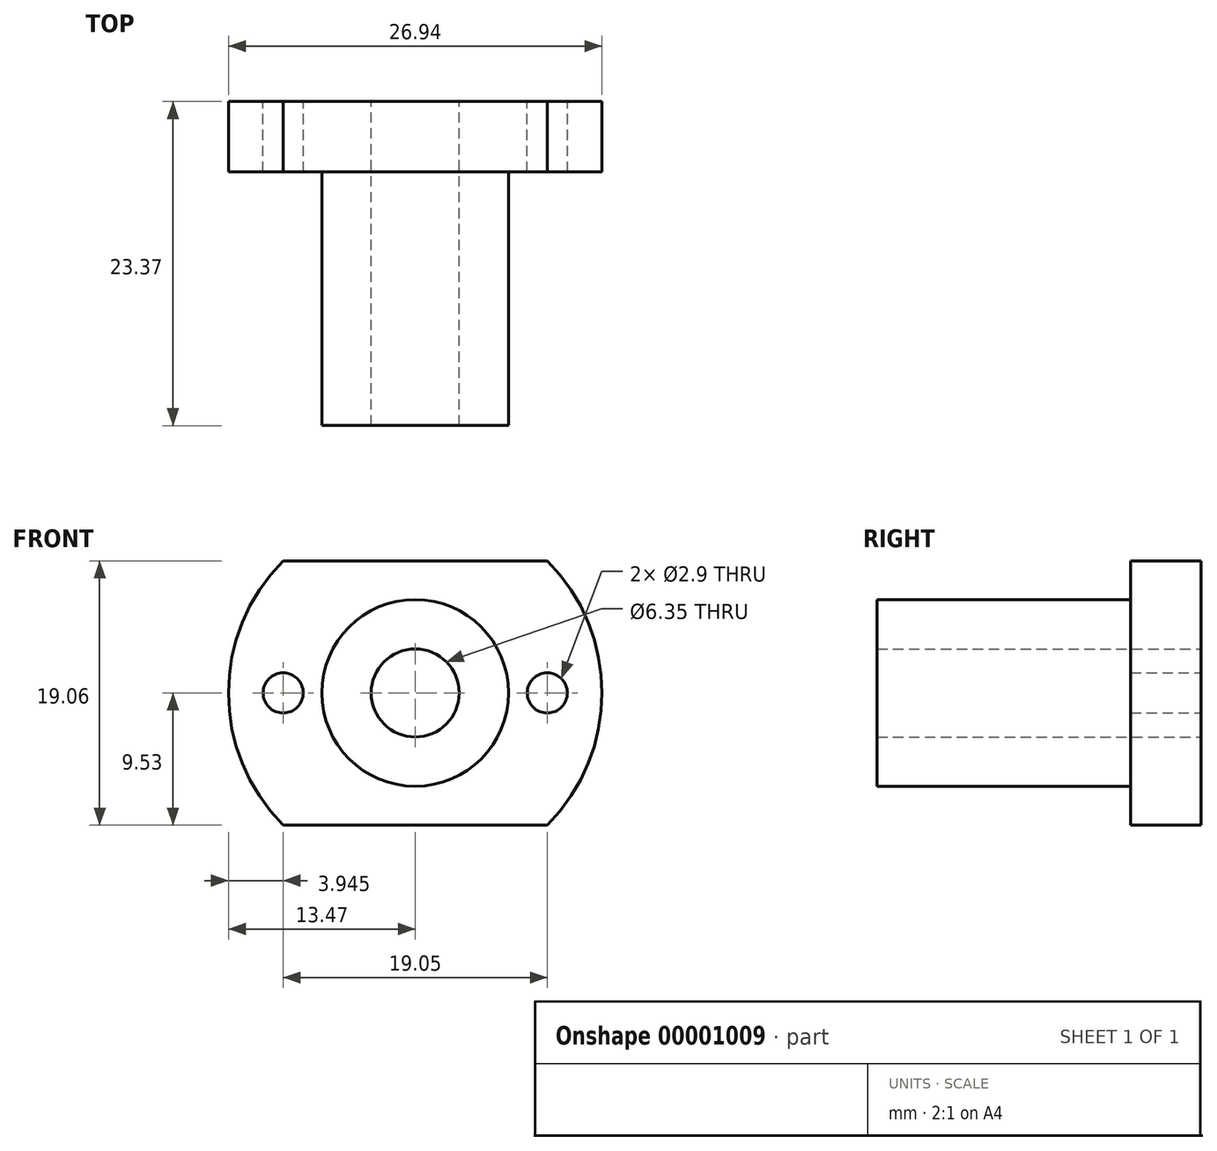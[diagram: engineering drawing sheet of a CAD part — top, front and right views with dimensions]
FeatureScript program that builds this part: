
annotation { "Feature Type Name" : "Feature", "Feature Type Description" : "" }
export const myFeature = defineFeature(function(context is Context, id is Id, definition is map)
    precondition{}
    {
        {
            var Q0;
            Q0=qCreatedBy(makeId("Front.planeOp"),FACE);
            var sketch = newSketch(context, id + "F0", { "sketchPlane" : qUnion([Q0])});
            skLineSegment(sketch, "E0.bottom", {"start": v(-9.53, 9.53) * mm, "end": v(9.53, 9.53) * mm});
            skLineSegment(sketch, "E0.top", {"start": v(-9.52, -9.53) * mm, "end": v(9.53, -9.52) * mm});
            skCircle(sketch, "E1", {"center": v(-9.53, 0) * mm, "radius": 1.45 * mm});
            skCircle(sketch, "E2", {"center": v(9.53, 0) * mm, "radius": 1.45 * mm});
            skArc(sketch, "E3", {"start": v(-9.53, 9.52) * mm, "mid": v(-13.47, 0) * mm, "end": v(-9.52, -9.53) * mm});
            skArc(sketch, "E4.trimOffspring", {"start": v(9.52, -9.52) * mm, "mid": v(13.47, 0) * mm, "end": v(9.52, 9.53) * mm});
            skCircle(sketch, "E5", {"center": v(0, 0) * mm, "radius": 3.18 * mm});
            skSolve(sketch);
        }
        {
            var Q0;
            Q0=makeQuery(id+"F0.imprint","IMPRINT",FACE,{"disambiguationData":[TD([[makeQuery(id+"F0.imprint","IMPRINT",EDGE,{"derivedFrom":sQuery(id+"F0.wireOp",EDGE,"E0.bottom")}),-1.0]])]});
            extrude(context, id + "F1", {"entities" : qUnion([Q0]), "depth" : 5.08 * mm});
        }
        {
            var Q0;
            Q0=makeQuery(id+"F1.opExtrude","CAP_FACE",FACE,{"disambiguationData":[OSD([sQuery(id+"F0.wireOp",EDGE,"E0.bottom"),sQuery(id+"F0.wireOp",EDGE,"E0.top"),sQuery(id+"F0.wireOp",EDGE,"E1"),sQuery(id+"F0.wireOp",EDGE,"E2"),sQuery(id+"F0.wireOp",EDGE,"E3"),sQuery(id+"F0.wireOp",EDGE,"E4.trimOffspring"),sQuery(id+"F0.wireOp",EDGE,"E5")])],"isStart":false});
            var sketch = newSketch(context, id + "F2", { "sketchPlane" : qUnion([Q0])});
            skCircle(sketch, "E6", {"center": v(0, 0) * mm, "radius": 6.73 * mm});
            skCircle(sketch, "E7", {"center": v(0, 0) * mm, "radius": 3.18 * mm});
            skSolve(sketch);
        }
        {
            var Q0;
            Q0=makeQuery(id+"F2.imprint","IMPRINT",FACE,{"disambiguationData":[TD([[makeQuery(id+"F2.imprint","IMPRINT",EDGE,{"derivedFrom":sQuery(id+"F2.wireOp",EDGE,"E6")}),1.0]])]});
            extrude(context, id + "F3", {"entities" : qUnion([Q0]), "operationType" : NewBodyOperationType.ADD, "depth" : 18.29 * mm});
        }
    });
